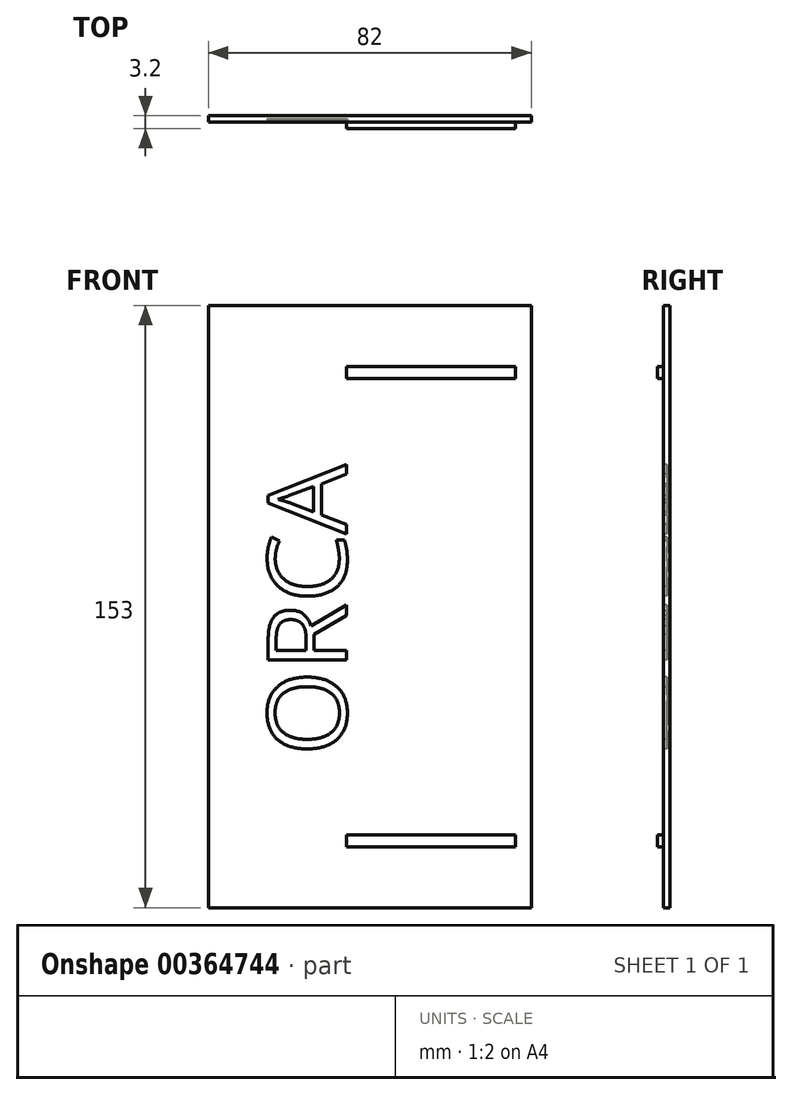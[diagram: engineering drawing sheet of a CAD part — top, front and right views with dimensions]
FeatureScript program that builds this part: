
annotation { "Feature Type Name" : "Feature", "Feature Type Description" : "" }
export const myFeature = defineFeature(function(context is Context, id is Id, definition is map)
    precondition{}
    {
        {
            var Q0;
            Q0=qCreatedBy(makeId("Front.planeOp"),FACE);
            var sketch = newSketch(context, id + "F0", { "sketchPlane" : qUnion([Q0])});
            skLineSegment(sketch, "E0", {"start": v(-82, 76.5) * mm, "end": v(0, 76.5) * mm});
            skLineSegment(sketch, "E1", {"start": v(0, 76.5) * mm, "end": v(0, -76.5) * mm});
            skLineSegment(sketch, "E2", {"start": v(0, -76.5) * mm, "end": v(-82, -76.5) * mm});
            skLineSegment(sketch, "E3", {"start": v(-82, -76.5) * mm, "end": v(-82, 76.5) * mm});
            skSolve(sketch);
        }
        {
            var Q0;
            Q0=qSketchRegion(id+"F0",true);
            extrude(context, id + "F1", {"entities" : qUnion([Q0]), "depth" : 1.6 * mm});
        }
        {
            var Q0;
            Q0=qCreatedBy(makeId("Front.planeOp"),FACE);
            cPlane(context, id + "F2", {"entities" : qUnion([Q0]), "cplaneType" : CPlaneType.OFFSET, "offset" : 1.6 * mm, "width" : 150 * mm, "height" : 150 * mm});
        }
        {
            var Q0;
            Q0=qCreatedBy(id+"F2.planeOp",FACE);
            var sketch = newSketch(context, id + "F3", { "sketchPlane" : qUnion([Q0])});
            skLineSegment(sketch, "E4", {"start": v(-4, 61) * mm, "end": v(-47, 61) * mm});
            skLineSegment(sketch, "E5", {"start": v(-4, 61) * mm, "end": v(-4, 58) * mm});
            skLineSegment(sketch, "E6", {"start": v(-4, 58) * mm, "end": v(-47, 58) * mm});
            skLineSegment(sketch, "E7", {"start": v(-47, 58) * mm, "end": v(-47, 61) * mm});
            skLineSegment(sketch, "E8.MirrorCS", {"start": v(-4, -58) * mm, "end": v(-47, -58) * mm});
            skLineSegment(sketch, "E9.MirrorCS", {"start": v(-4, -61) * mm, "end": v(-4, -58) * mm});
            skLineSegment(sketch, "E10.MirrorCS", {"start": v(-47, -58) * mm, "end": v(-47, -61) * mm});
            skLineSegment(sketch, "E11.MirrorCS", {"start": v(-4, -61) * mm, "end": v(-47, -61) * mm});
            skSolve(sketch);
        }
        {
            var Q0;
            Q0=qSketchRegion(id+"F3",true);
            extrude(context, id + "F4", {"entities" : qUnion([Q0]), "operationType" : NewBodyOperationType.ADD, "depth" : 1.6 * mm});
        }
        {
            var Q0;
            Q0=makeQuery(id+"F1.opExtrude","CAP_FACE",FACE,{"disambiguationData":[OSD([sQuery(id+"F0.wireOp",EDGE,"E0"),sQuery(id+"F0.wireOp",EDGE,"E1"),sQuery(id+"F0.wireOp",EDGE,"E2"),sQuery(id+"F0.wireOp",EDGE,"E3")])],"isStart":false});
            var sketch = newSketch(context, id + "F5", { "sketchPlane" : qUnion([Q0])});
            skText(sketch, "E12", { "text": "ORCA", "fontName": "OpenSans-Regular.ttf"});
            const initialGuessF5  = {"E12": [-0.047, -0.03785, 0, 1, 0.02]};
            skSetInitialGuess(sketch, initialGuessF5);
            skSolve(sketch);
        }
        {
            var Q0;
            Q0=qSketchRegion(id+"F5",true);
            extrude(context, id + "F6", {"entities" : qUnion([Q0]), "operationType" : NewBodyOperationType.REMOVE, "oppositeDirection" : true, "depth" : .8 * mm});
        }
    });
